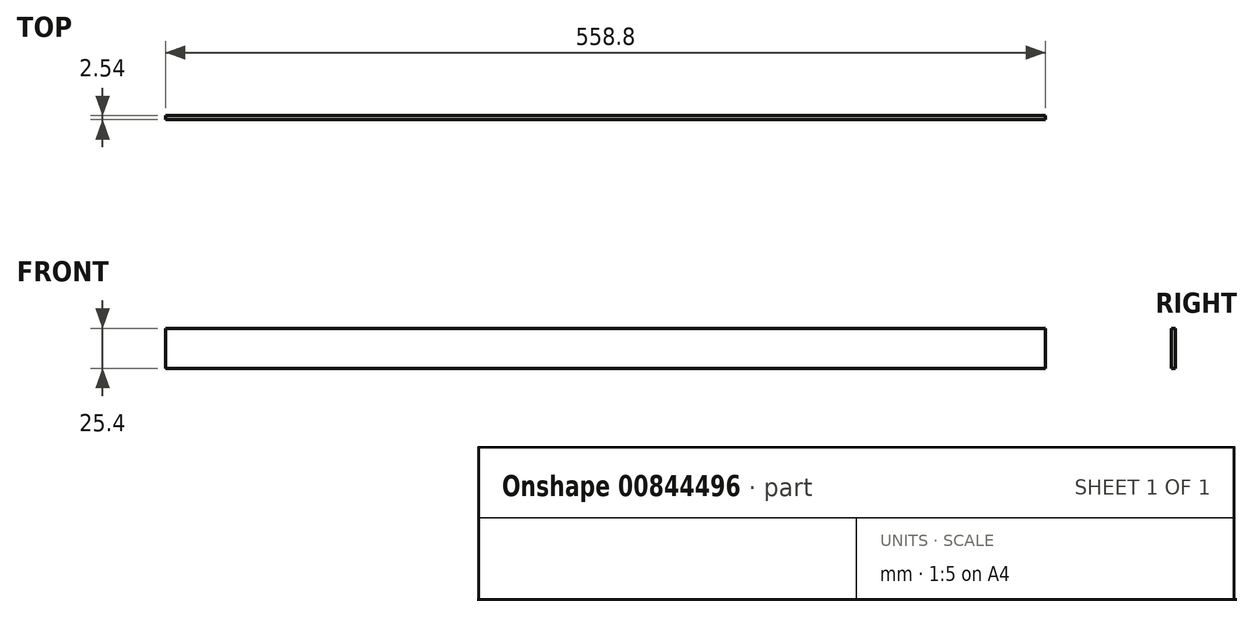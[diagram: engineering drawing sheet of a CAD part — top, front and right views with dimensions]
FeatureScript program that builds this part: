
annotation { "Feature Type Name" : "Feature", "Feature Type Description" : "" }
export const myFeature = defineFeature(function(context is Context, id is Id, definition is map)
    precondition{}
    {
        {
            var Q0;
            Q0=qCreatedBy(makeId("Right.planeOp"),FACE);
            var sketch = newSketch(context, id + "F0", { "sketchPlane" : qUnion([Q0])});
            skLineSegment(sketch, "E0.bottom", {"start": v(1.27, 12.7) * mm, "end": v(-1.27, 12.7) * mm});
            skLineSegment(sketch, "E0.top", {"start": v(1.27, -12.7) * mm, "end": v(-1.27, -12.7) * mm});
            skLineSegment(sketch, "E0.left", {"start": v(1.27, 12.7) * mm, "end": v(1.27, -12.7) * mm});
            skLineSegment(sketch, "E0.right", {"start": v(-1.27, 12.7) * mm, "end": v(-1.27, -12.7) * mm});
            skPoint(sketch, "E0.middle", {"position": v(0, 0) * mm});
            skSolve(sketch);
        }
        {
            var Q0;
            Q0 = qSketchRegion(id + "F0", true);
            extrude(context, id + "F1", {"entities" : qUnion([Q0]), "depth" : 558.8 * mm, "offsetDistance" : 25.4 * mm, "symmetric" : true});
        }
    });
